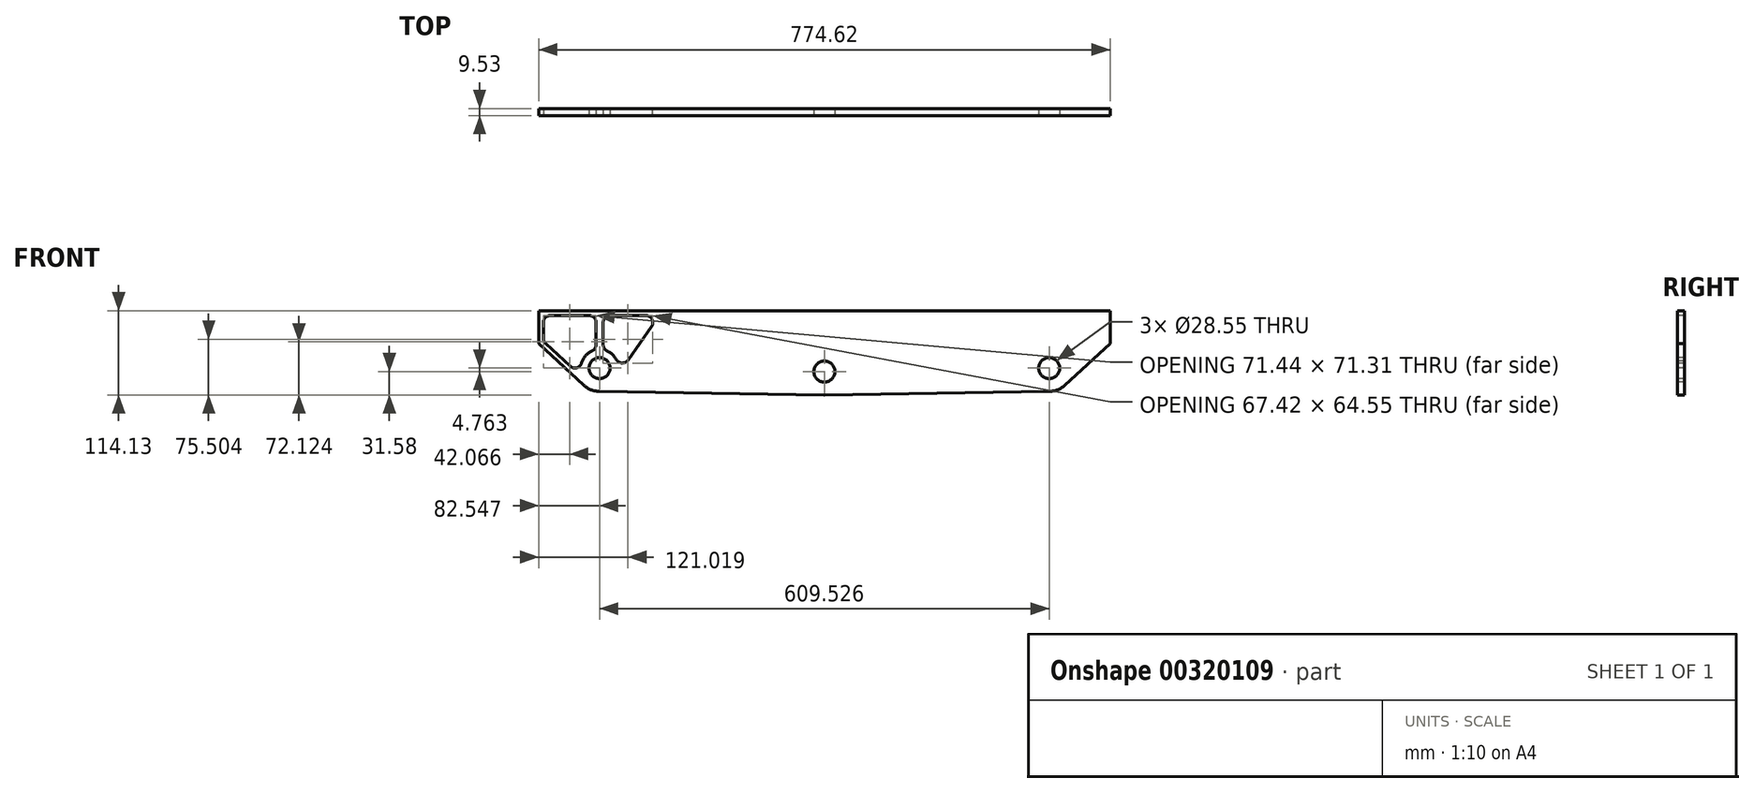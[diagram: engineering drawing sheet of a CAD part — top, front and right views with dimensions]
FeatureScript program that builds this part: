
annotation { "Feature Type Name" : "Feature", "Feature Type Description" : "" }
export const myFeature = defineFeature(function(context is Context, id is Id, definition is map)
    precondition{}
    {
        {
            var Q0;
            Q0=qCreatedBy(makeId("Front.planeOp"),FACE);
            var sketch = newSketch(context, id + "F0", { "sketchPlane" : qUnion([Q0])});
            skCircle(sketch, "E0", {"center": v(0, 0) * mm, "radius": 76.2 * mm, "construction": true});
            skLineSegment(sketch, "E1", {"start": v(2266.68, -76.2) * mm, "end": v(-1114.7, -76.2) * mm, "construction": true});
            skCircle(sketch, "E2", {"center": v(0, 0) * mm, "radius": 22.24 * mm, "construction": true});
            skCircle(sketch, "E3", {"center": v(304.76, 4.76) * mm, "radius": 22.24 * mm, "construction": true});
            skCircle(sketch, "E4", {"center": v(304.76, 4.76) * mm, "radius": 76.2 * mm, "construction": true});
            skCircle(sketch, "E5", {"center": v(-304.76, 4.76) * mm, "radius": 22.24 * mm, "construction": true});
            skCircle(sketch, "E6", {"center": v(-304.76, 4.76) * mm, "radius": 76.2 * mm, "construction": true});
            skLineSegment(sketch, "E7", {"start": v(-304.42, 27) * mm, "end": v(0.35, 22.23) * mm, "construction": true});
            skLineSegment(sketch, "E8", {"start": v(-0.35, -22.23) * mm, "end": v(-305.11, -17.47) * mm, "construction": true});
            skLineSegment(sketch, "E9", {"start": v(-0.35, 22.23) * mm, "end": v(304.42, 27) * mm, "construction": true});
            skLineSegment(sketch, "E10", {"start": v(305.11, -17.47) * mm, "end": v(0.35, -22.23) * mm, "construction": true});
            skLineSegment(sketch, "E11.bottom", {"start": v(-387.31, 82.55) * mm, "end": v(387.31, 82.55) * mm});
            skLineSegment(sketch, "E11.left", {"start": v(-387.31, 82.55) * mm, "end": v(-387.31, 38.1) * mm});
            skLineSegment(sketch, "E11.right", {"start": v(387.31, 82.55) * mm, "end": v(387.31, 38.1) * mm});
            skArc(sketch, "E12", {"start": v(-326.21, -18.42) * mm, "mid": v(-316.5, -24.56) * mm, "end": v(-305.26, -26.82) * mm});
            skArc(sketch, "E13", {"start": v(-0.5, -31.58) * mm, "mid": v(0, -31.58) * mm, "end": v(0.5, -31.58) * mm});
            skArc(sketch, "E14", {"start": v(305.26, -26.82) * mm, "mid": v(316.5, -24.56) * mm, "end": v(326.21, -18.42) * mm});
            skCircle(sketch, "E15", {"center": v(-304.76, 4.76) * mm, "radius": 25.23 * mm, "construction": true});
            skLineSegment(sketch, "E16", {"start": v(-387.31, 38.1) * mm, "end": v(-326.21, -18.42) * mm});
            skLineSegment(sketch, "E17", {"start": v(-305.26, -26.82) * mm, "end": v(-0.5, -31.58) * mm});
            skLineSegment(sketch, "E18.trimOffspring", {"start": v(0.5, -31.58) * mm, "end": v(305.26, -26.82) * mm});
            skLineSegment(sketch, "E19", {"start": v(387.31, 38.1) * mm, "end": v(326.21, -18.42) * mm});
            skSolve(sketch);
        }
        {
            var Q0;
            Q0 = qSketchRegion(id + "F0", true);
            extrude(context, id + "F1", {"entities" : qUnion([Q0]), "depth" : 9.52 * mm});
        }
        {
            var Q0;
            Q0=makeQuery(id+"F1.opExtrude","CAP_FACE",FACE,{"disambiguationData":[OSD([sQuery(id+"F0.wireOp",EDGE,"E11.bottom"),sQuery(id+"F0.wireOp",EDGE,"E11.left"),sQuery(id+"F0.wireOp",EDGE,"E11.right"),sQuery(id+"F0.wireOp",EDGE,"E12"),sQuery(id+"F0.wireOp",EDGE,"E13"),sQuery(id+"F0.wireOp",EDGE,"E14"),sQuery(id+"F0.wireOp",EDGE,"E16"),sQuery(id+"F0.wireOp",EDGE,"E17"),sQuery(id+"F0.wireOp",EDGE,"E18.trimOffspring"),sQuery(id+"F0.wireOp",EDGE,"E19")])],"isStart":false});
            var sketch = newSketch(context, id + "F2", { "sketchPlane" : qUnion([Q0])});
            skCircle(sketch, "E20", {"center": v(-304.76, 4.76) * mm, "radius": 14.27 * mm});
            skCircle(sketch, "E21", {"center": v(0, 0) * mm, "radius": 14.27 * mm});
            skCircle(sketch, "E22", {"center": v(304.76, 4.76) * mm, "radius": 14.27 * mm});
            skLineSegment(sketch, "E23", {"start": v(-380.96, 76.2) * mm, "end": v(-380.96, 40.88) * mm});
            skLineSegment(sketch, "E24", {"start": v(-380.96, 40.88) * mm, "end": v(-324.02, -11.8) * mm});
            skLineSegment(sketch, "E25", {"start": v(-380.96, 76.2) * mm, "end": v(-309.53, 76.2) * mm});
            skLineSegment(sketch, "E26", {"start": v(-309.53, 76.2) * mm, "end": v(-309.53, 29.71) * mm});
            skCircle(sketch, "E27", {"center": v(-304.76, 4.76) * mm, "radius": 25.4 * mm, "construction": true});
            skLineSegment(sketch, "E28", {"start": v(-300, 29.71) * mm, "end": v(-300, 76.2) * mm});
            skLineSegment(sketch, "E29", {"start": v(-300, 76.2) * mm, "end": v(-223.8, 76.2) * mm});
            skLineSegment(sketch, "E30", {"start": v(-223.8, 76.2) * mm, "end": v(-283.95, -9.8) * mm});
            skLineSegment(sketch, "E31", {"start": v(-304.76, 4.76) * mm, "end": v(-304.76, 82.55) * mm, "construction": true});
            skArc(sketch, "E32", {"start": v(-283.95, -9.8) * mm, "mid": v(-281.23, 14.32) * mm, "end": v(-300, 29.71) * mm});
            skArc(sketch, "E33", {"start": v(-309.53, 29.71) * mm, "mid": v(-328.74, 13.14) * mm, "end": v(-324.02, -11.8) * mm});
            skSolve(sketch);
        }
        {
            var Q0;
            Q0 = qSketchRegion(id + "F2", true);
            extrude(context, id + "F3", {"entities" : qUnion([Q0]), "operationType" : NewBodyOperationType.REMOVE, "oppositeDirection" : true, "depth" : 25.4 * mm});
        }
        {
            var Q0;
            Q0=makeQuery(id+"F3.boolean.opBoolean","COPY",EDGE,{"derivedFrom":makeQuery(id+"F3.opExtrude","SWEPT_EDGE",EDGE,{"disambiguationData":[OSD([sQuery(id+"F2.wireOp",EDGE,"E28"),sQuery(id+"F2.wireOp",EDGE,"E32")])]})});
            var Q1;
            Q1=makeQuery(id+"F3.boolean.opBoolean","COPY",EDGE,{"derivedFrom":makeQuery(id+"F3.opExtrude","SWEPT_EDGE",EDGE,{"disambiguationData":[OSD([sQuery(id+"F2.wireOp",EDGE,"E28"),sQuery(id+"F2.wireOp",EDGE,"E29")])]})});
            var Q2;
            Q2=makeQuery(id+"F3.boolean.opBoolean","COPY",EDGE,{"derivedFrom":makeQuery(id+"F3.opExtrude","SWEPT_EDGE",EDGE,{"disambiguationData":[OSD([sQuery(id+"F2.wireOp",EDGE,"E29"),sQuery(id+"F2.wireOp",EDGE,"E30")])]})});
            var Q3;
            Q3=makeQuery(id+"F3.boolean.opBoolean","COPY",EDGE,{"derivedFrom":makeQuery(id+"F3.opExtrude","SWEPT_EDGE",EDGE,{"disambiguationData":[OSD([sQuery(id+"F2.wireOp",EDGE,"E30"),sQuery(id+"F2.wireOp",EDGE,"E32")])]})});
            var Q4;
            Q4=makeQuery(id+"F3.boolean.opBoolean","COPY",EDGE,{"derivedFrom":makeQuery(id+"F3.opExtrude","SWEPT_EDGE",EDGE,{"disambiguationData":[OSD([sQuery(id+"F2.wireOp",EDGE,"E26"),sQuery(id+"F2.wireOp",EDGE,"E33")])]})});
            var Q5;
            Q5=makeQuery(id+"F3.boolean.opBoolean","COPY",EDGE,{"derivedFrom":makeQuery(id+"F3.opExtrude","SWEPT_EDGE",EDGE,{"disambiguationData":[OSD([sQuery(id+"F2.wireOp",EDGE,"E24"),sQuery(id+"F2.wireOp",EDGE,"E33")])]})});
            var Q6;
            Q6=makeQuery(id+"F3.boolean.opBoolean","COPY",EDGE,{"derivedFrom":makeQuery(id+"F3.opExtrude","SWEPT_EDGE",EDGE,{"disambiguationData":[OSD([sQuery(id+"F2.wireOp",EDGE,"E23"),sQuery(id+"F2.wireOp",EDGE,"E24")])]})});
            var Q7;
            Q7=makeQuery(id+"F3.boolean.opBoolean","COPY",EDGE,{"derivedFrom":makeQuery(id+"F3.opExtrude","SWEPT_EDGE",EDGE,{"disambiguationData":[OSD([sQuery(id+"F2.wireOp",EDGE,"E23"),sQuery(id+"F2.wireOp",EDGE,"E25")])]})});
            var Q8;
            Q8=makeQuery(id+"F3.boolean.opBoolean","COPY",EDGE,{"derivedFrom":makeQuery(id+"F3.opExtrude","SWEPT_EDGE",EDGE,{"disambiguationData":[OSD([sQuery(id+"F2.wireOp",EDGE,"E25"),sQuery(id+"F2.wireOp",EDGE,"E26")])]})});
            fillet(context, id + "F4", {"entities" : qUnion([Q0, Q1, Q2, Q3, Q4, Q5, Q6, Q7, Q8]), "radius" : 9.52 * mm, "tangentPropagation" : true, "allowEdgeOverflow" : false});
        }
    });
